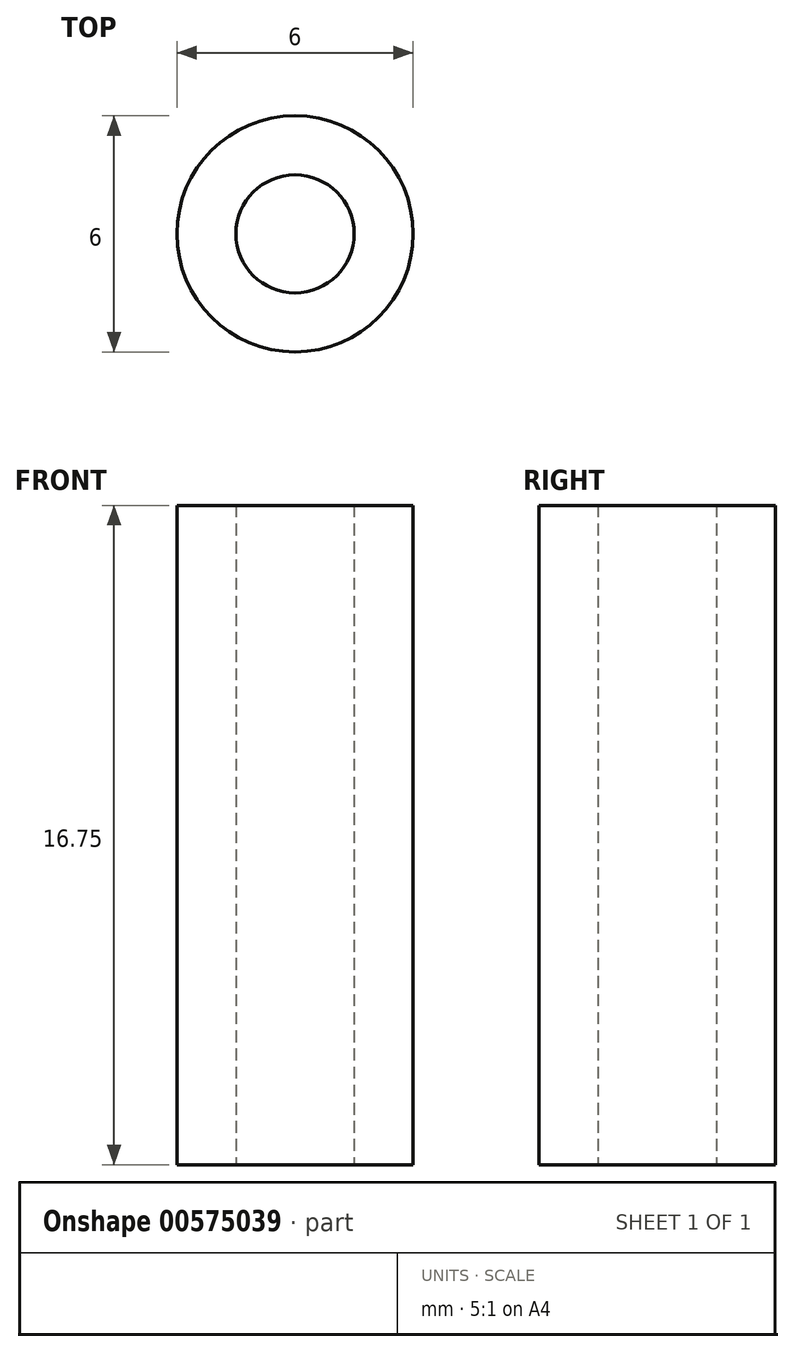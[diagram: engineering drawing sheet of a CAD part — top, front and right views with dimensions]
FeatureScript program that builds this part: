
annotation { "Feature Type Name" : "Feature", "Feature Type Description" : "" }
export const myFeature = defineFeature(function(context is Context, id is Id, definition is map)
    precondition{}
    {
        {
            var Q0;
            Q0=qCreatedBy(makeId("Top.planeOp"),FACE);
            var sketch = newSketch(context, id + "F0", { "sketchPlane" : qUnion([Q0])});
            skCircle(sketch, "E0", {"center": v(0, 0) * mm, "radius": 3 * mm});
            skCircle(sketch, "E1", {"center": v(0, 0) * mm, "radius": 1.5 * mm});
            skSolve(sketch);
        }
        {
            var Q0;
            Q0 = qSketchRegion(id + "F0", true);
            extrude(context, id + "F1", {"entities" : qUnion([Q0]), "depth" : 16.75 * mm, "offsetDistance" : 25 * mm});
        }
    });
